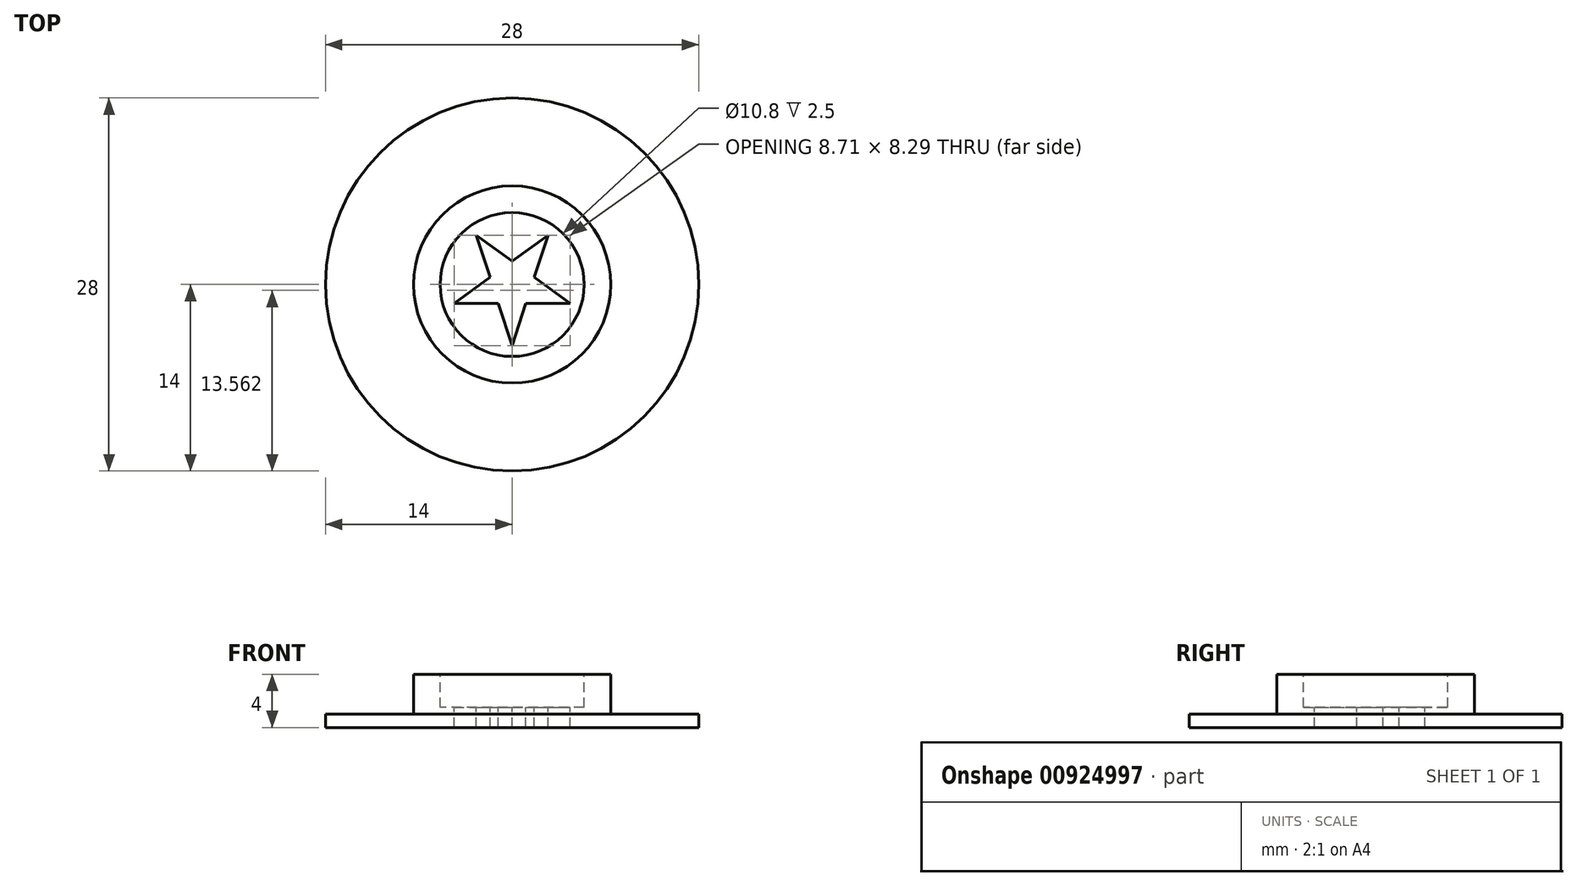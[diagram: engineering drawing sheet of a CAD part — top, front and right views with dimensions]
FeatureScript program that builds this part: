
annotation { "Feature Type Name" : "Feature", "Feature Type Description" : "" }
export const myFeature = defineFeature(function(context is Context, id is Id, definition is map)
    precondition{}
    {
        {
            var Q0;
            Q0=qCreatedBy(makeId("Front.planeOp"),FACE);
            var sketch = newSketch(context, id + "F0", { "sketchPlane" : qUnion([Q0])});
            skLineSegment(sketch, "E0", {"start": v(0, 0) * mm, "end": v(14, 0) * mm});
            skLineSegment(sketch, "E1", {"start": v(14, 0) * mm, "end": v(14, 1) * mm});
            skLineSegment(sketch, "E2", {"start": v(14, 1) * mm, "end": v(7.4, 1) * mm});
            skLineSegment(sketch, "E3", {"start": v(7.4, 1) * mm, "end": v(7.4, 4) * mm});
            skLineSegment(sketch, "E4", {"start": v(7.4, 4) * mm, "end": v(5.4, 4) * mm});
            skLineSegment(sketch, "E5", {"start": v(0, 1.5) * mm, "end": v(0, 0) * mm});
            skLineSegment(sketch, "E6", {"start": v(5.4, 4) * mm, "end": v(5.4, 1.5) * mm});
            skLineSegment(sketch, "E7", {"start": v(5.4, 1.5) * mm, "end": v(0, 1.5) * mm});
            skSolve(sketch);
        }
        {
            var Q0;
            Q0 = qSketchRegion(id + "F0", true);
            var Q1;
            Q1=sQuery(id+"F0.wireOp",EDGE,"E5");
            revolve(context, id + "F1", {"surfaceOperationType" : NewSurfaceOperationType.NEW, "entities" : qUnion([Q0]), "axis" : qUnion([Q1]), "revolveType" : RevolveType.FULL});
        }
        {
            var Q0;
            Q0=makeQuery(id+"F1.opRevolve","SWEPT_FACE",FACE,{"disambiguationData":[OSD([sQuery(id+"F0.wireOp",EDGE,"E7")])]});
            var sketch = newSketch(context, id + "F2", { "sketchPlane" : qUnion([Q0])});
            skCircle(sketch, "E8.cCircle", {"center": v(0, 0) * mm, "radius": 3.7 * mm, "construction": true});
            skLineSegment(sketch, "E8.0", {"start": v(-2.7, 3.7) * mm, "end": v(2.7, 3.7) * mm, "construction": true});
            skLineSegment(sketch, "E8.1", {"start": v(2.7, 3.7) * mm, "end": v(4.36, -1.42) * mm, "construction": true});
            skLineSegment(sketch, "E8.2", {"start": v(4.36, -1.42) * mm, "end": v(0, -4.58) * mm, "construction": true});
            skLineSegment(sketch, "E8.3", {"start": v(0, -4.58) * mm, "end": v(-4.36, -1.42) * mm, "construction": true});
            skLineSegment(sketch, "E8.4", {"start": v(-4.36, -1.42) * mm, "end": v(-2.7, 3.7) * mm, "construction": true});
            skPoint(sketch, "E8.0.midPoint", {"position": v(0, 3.7) * mm});
            skLineSegment(sketch, "E9", {"start": v(-2.7, 3.7) * mm, "end": v(4.36, -1.42) * mm});
            skLineSegment(sketch, "E10", {"start": v(-4.36, -1.42) * mm, "end": v(2.7, 3.7) * mm});
            skLineSegment(sketch, "E11", {"start": v(0, -4.58) * mm, "end": v(2.7, 3.7) * mm});
            skLineSegment(sketch, "E12", {"start": v(-2.7, 3.7) * mm, "end": v(0, -4.58) * mm});
            skLineSegment(sketch, "E13", {"start": v(-4.36, -1.42) * mm, "end": v(4.36, -1.42) * mm});
            skSolve(sketch);
        }
        {
            var Q0;
            {var subQ0=sQuery(id+"F2.wireOp",EDGE,"E13");var subQ1=sQuery(id+"F2.wireOp",EDGE,"E10");var subQ2=makeQuery(id+"F2.imprint","INTERSECT",VERTEX,{"derivedFrom":[subQ1,subQ0]});Q0=makeQuery(id+"F2.imprint","IMPRINT",FACE,{"disambiguationData":[TD([[makeQuery(id+"F2.imprint","IMPRINT",EDGE,{"disambiguationData":[TD([[subQ2,-1.0]])],"derivedFrom":subQ1}),-1.0]])]});}
            var Q1;
            {var subQ0=sQuery(id+"F2.wireOp",EDGE,"E12");var subQ1=sQuery(id+"F2.wireOp",EDGE,"E9");var subQ2=makeQuery(id+"F2.imprint","INTERSECT",VERTEX,{"derivedFrom":[subQ1,subQ0]});Q1=makeQuery(id+"F2.imprint","IMPRINT",FACE,{"disambiguationData":[TD([[makeQuery(id+"F2.imprint","IMPRINT",EDGE,{"disambiguationData":[TD([[subQ2,-1.0]])],"derivedFrom":subQ1}),-1.0]])]});}
            var Q2;
            {var subQ1=sQuery(id+"F2.wireOp",EDGE,"E10");var subQ6=sQuery(id+"F2.wireOp",EDGE,"E9");var subQ9=makeQuery(id+"F2.imprint","INTERSECT",VERTEX,{"derivedFrom":[subQ6,subQ1]});Q2=makeQuery(id+"F2.imprint","IMPRINT",FACE,{"disambiguationData":[TD([[makeQuery(id+"F2.imprint","IMPRINT",EDGE,{"disambiguationData":[TD([[subQ9,-1.0]])],"derivedFrom":subQ6}),-1.0]])]});}
            var Q3;
            {var subQ0=sQuery(id+"F2.wireOp",EDGE,"E10");var subQ1=sQuery(id+"F2.wireOp",EDGE,"E9");var subQ2=makeQuery(id+"F2.imprint","INTERSECT",VERTEX,{"derivedFrom":[subQ1,subQ0]});Q3=makeQuery(id+"F2.imprint","IMPRINT",FACE,{"disambiguationData":[TD([[makeQuery(id+"F2.imprint","IMPRINT",EDGE,{"disambiguationData":[TD([[subQ2,-1.0]])],"derivedFrom":subQ1}),1.0]])]});}
            var Q4;
            {var subQ0=sQuery(id+"F2.wireOp",EDGE,"E13");var subQ1=sQuery(id+"F2.wireOp",EDGE,"E9");var subQ2=makeQuery(id+"F2.imprint","INTERSECT",VERTEX,{"derivedFrom":[subQ1,subQ0]});Q4=makeQuery(id+"F2.imprint","IMPRINT",FACE,{"disambiguationData":[TD([[makeQuery(id+"F2.imprint","IMPRINT",EDGE,{"disambiguationData":[TD([[subQ2,1.0]])],"derivedFrom":subQ1}),-1.0]])]});}
            var Q5;
            {var subQ0=sQuery(id+"F2.wireOp",EDGE,"E12");var subQ1=sQuery(id+"F2.wireOp",EDGE,"E11");var subQ2=makeQuery(id+"F2.imprint","INTERSECT",VERTEX,{"derivedFrom":[subQ1,subQ0]});Q5=makeQuery(id+"F2.imprint","IMPRINT",FACE,{"disambiguationData":[TD([[makeQuery(id+"F2.imprint","IMPRINT",EDGE,{"disambiguationData":[TD([[subQ2,-1.0]])],"derivedFrom":subQ1}),1.0]])]});}
            extrude(context, id + "F3", {"entities" : qUnion([Q0, Q1, Q2, Q3, Q4, Q5]), "operationType" : NewBodyOperationType.REMOVE, "oppositeDirection" : true, "depth" : 25 * mm, "offsetDistance" : 25 * mm});
        }
    });
